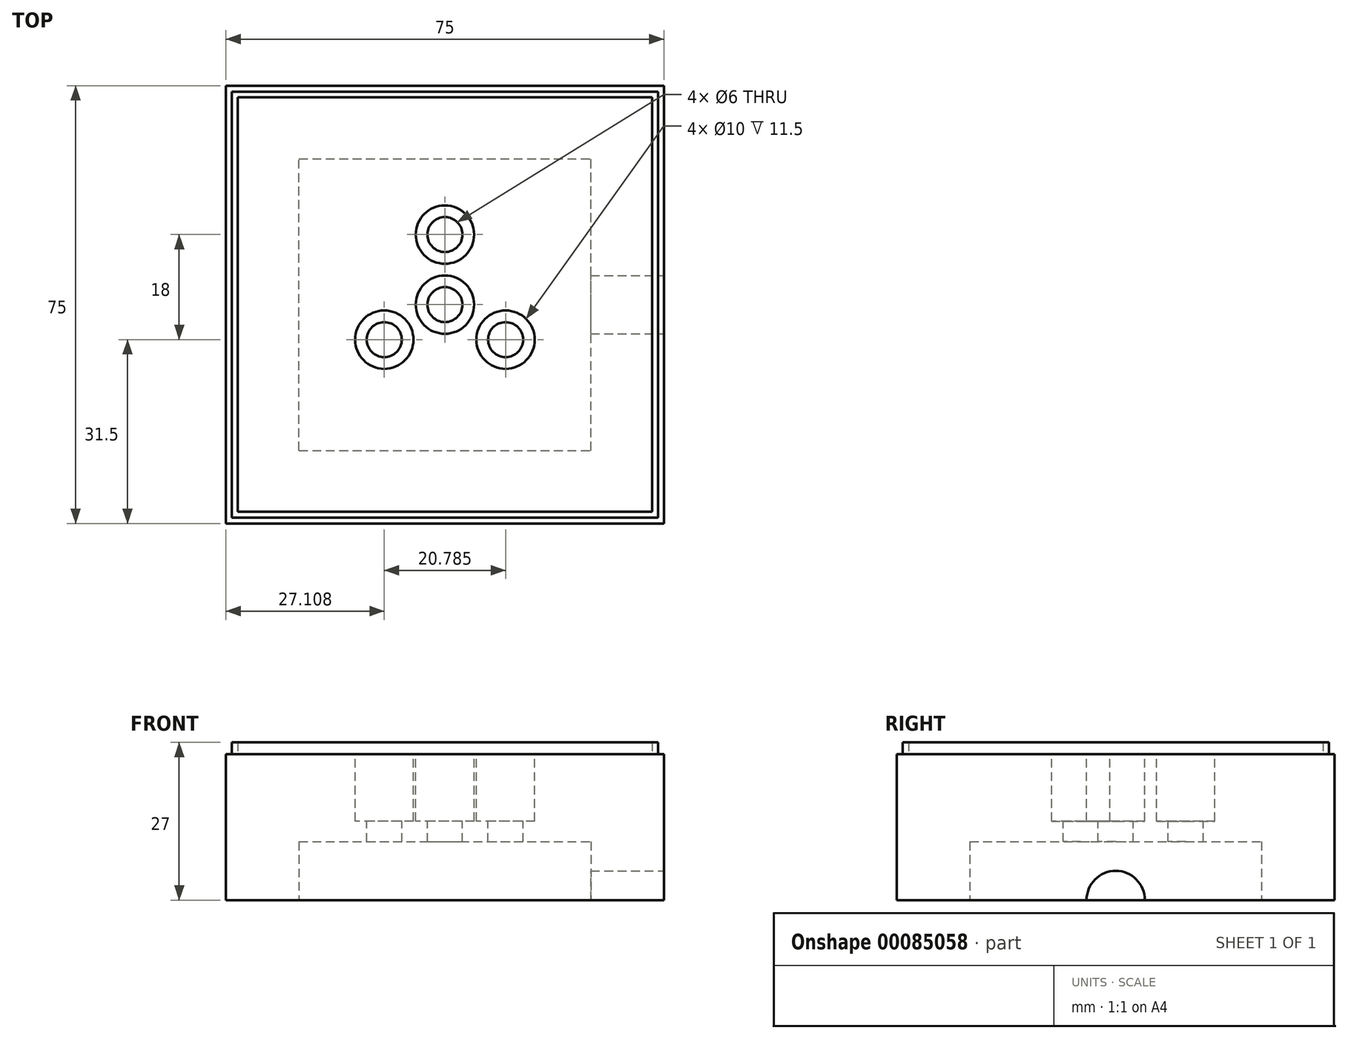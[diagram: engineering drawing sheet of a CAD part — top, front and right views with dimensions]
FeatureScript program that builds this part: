
annotation { "Feature Type Name" : "Feature", "Feature Type Description" : "" }
export const myFeature = defineFeature(function(context is Context, id is Id, definition is map)
    precondition{}
    {
        {
            var Q0;
            Q0=qCreatedBy(makeId("Top.planeOp"),FACE);
            var sketch = newSketch(context, id + "F0", { "sketchPlane" : qUnion([Q0])});
            skLineSegment(sketch, "E0.bottom", {"start": v(37.5, 37.5) * mm, "end": v(-37.5, 37.5) * mm});
            skLineSegment(sketch, "E0.top", {"start": v(37.5, -37.5) * mm, "end": v(-37.5, -37.5) * mm});
            skLineSegment(sketch, "E0.left", {"start": v(37.5, 37.5) * mm, "end": v(37.5, -37.5) * mm});
            skLineSegment(sketch, "E0.right", {"start": v(-37.5, 37.5) * mm, "end": v(-37.5, -37.5) * mm});
            skPoint(sketch, "E0.middle", {"position": v(0, 0) * mm});
            skSolve(sketch);
        }
        {
            var Q0;
            Q0 = qSketchRegion(id + "F0", true);
            extrude(context, id + "F1", {"entities" : qUnion([Q0]), "depth" : 25 * mm});
        }
        {
            var Q0;
            Q0=makeQuery(id+"F1.opExtrude","CAP_FACE",FACE,{"disambiguationData":[OSD([sQuery(id+"F0.wireOp",EDGE,"E0.bottom"),sQuery(id+"F0.wireOp",EDGE,"E0.top"),sQuery(id+"F0.wireOp",EDGE,"E0.left"),sQuery(id+"F0.wireOp",EDGE,"E0.right")])],"isStart":false});
            var sketch = newSketch(context, id + "F2", { "sketchPlane" : qUnion([Q0])});
            skLineSegment(sketch, "E1.bottom", {"start": v(35.5, 35.5) * mm, "end": v(-35.5, 35.5) * mm});
            skLineSegment(sketch, "E1.top", {"start": v(35.5, -35.5) * mm, "end": v(-35.5, -35.5) * mm});
            skLineSegment(sketch, "E1.left", {"start": v(35.5, 35.5) * mm, "end": v(35.5, -35.5) * mm});
            skLineSegment(sketch, "E1.right", {"start": v(-35.5, 35.5) * mm, "end": v(-35.5, -35.5) * mm});
            skPoint(sketch, "E1.middle", {"position": v(0, 0) * mm});
            skLineSegment(sketch, "E2.0", {"start": v(36.5, 36.5) * mm, "end": v(-36.5, 36.5) * mm});
            skLineSegment(sketch, "E2.1", {"start": v(36.5, 36.5) * mm, "end": v(36.5, -36.5) * mm});
            skLineSegment(sketch, "E2.2", {"start": v(36.5, -36.5) * mm, "end": v(-36.5, -36.5) * mm});
            skLineSegment(sketch, "E2.3", {"start": v(-36.5, 36.5) * mm, "end": v(-36.5, -36.5) * mm});
            skSolve(sketch);
        }
        {
            var Q0;
            Q0 = qSketchRegion(id + "F2", true);
            extrude(context, id + "F3", {"entities" : qUnion([Q0]), "operationType" : NewBodyOperationType.ADD, "depth" : 2 * mm});
        }
        {
            var Q0;
            Q0=makeQuery(id+"F3.boolean.opBoolean","SPLIT",FACE,{"disambiguationData":[TD([makeQuery(id+"F3.opExtrude","SWEPT_FACE",FACE,{"disambiguationData":[OSD([sQuery(id+"F2.wireOp",EDGE,"E1.bottom")])]})])],"derivedFrom":makeQuery(id+"F1.opExtrude","CAP_FACE",FACE,{"disambiguationData":[OSD([sQuery(id+"F0.wireOp",EDGE,"E0.bottom"),sQuery(id+"F0.wireOp",EDGE,"E0.top"),sQuery(id+"F0.wireOp",EDGE,"E0.left"),sQuery(id+"F0.wireOp",EDGE,"E0.right")])],"isStart":false})});
            var sketch = newSketch(context, id + "F4", { "sketchPlane" : qUnion([Q0])});
            skCircle(sketch, "E3", {"center": v(0, 0) * mm, "radius": 3 * mm});
            skLineSegment(sketch, "E4", {"start": v(0, 0) * mm, "end": v(0, 12) * mm});
            skCircle(sketch, "E5", {"center": v(0, 12) * mm, "radius": 3 * mm});
            skCircle(sketch, "E6.1.0", {"center": v(-10.4, -6) * mm, "radius": 3 * mm});
            skCircle(sketch, "E6.2.0", {"center": v(10.4, -6) * mm, "radius": 3 * mm});
            skSolve(sketch);
        }
        {
            var Q0;
            Q0 = qSketchRegion(id + "F4", true);
            extrude(context, id + "F5", {"entities" : qUnion([Q0]), "operationType" : NewBodyOperationType.REMOVE, "oppositeDirection" : true, "depth" : 20 * mm});
        }
        {
            var Q0;
            Q0=makeQuery(id+"F3.boolean.opBoolean","SPLIT",FACE,{"disambiguationData":[TD([makeQuery(id+"F3.opExtrude","SWEPT_FACE",FACE,{"disambiguationData":[OSD([sQuery(id+"F2.wireOp",EDGE,"E1.bottom")])]})])],"derivedFrom":makeQuery(id+"F1.opExtrude","CAP_FACE",FACE,{"disambiguationData":[OSD([sQuery(id+"F0.wireOp",EDGE,"E0.bottom"),sQuery(id+"F0.wireOp",EDGE,"E0.top"),sQuery(id+"F0.wireOp",EDGE,"E0.left"),sQuery(id+"F0.wireOp",EDGE,"E0.right")])],"isStart":false})});
            var sketch = newSketch(context, id + "F6", { "sketchPlane" : qUnion([Q0])});
            skCircle(sketch, "E7", {"center": v(0, 0) * mm, "radius": 5 * mm});
            skCircle(sketch, "E8", {"center": v(0, 12) * mm, "radius": 5 * mm});
            skCircle(sketch, "E9.1.0", {"center": v(-10.4, -6) * mm, "radius": 5 * mm});
            skCircle(sketch, "E9.2.0", {"center": v(10.4, -6) * mm, "radius": 5 * mm});
            skSolve(sketch);
        }
        {
            var Q0;
            Q0 = qSketchRegion(id + "F6", true);
            extrude(context, id + "F7", {"entities" : qUnion([Q0]), "operationType" : NewBodyOperationType.REMOVE, "oppositeDirection" : true, "depth" : 11.5 * mm});
        }
        {
            var Q0;
            Q0=makeQuery(id+"F1.opExtrude","CAP_FACE",FACE,{"disambiguationData":[OSD([sQuery(id+"F0.wireOp",EDGE,"E0.bottom"),sQuery(id+"F0.wireOp",EDGE,"E0.top"),sQuery(id+"F0.wireOp",EDGE,"E0.left"),sQuery(id+"F0.wireOp",EDGE,"E0.right")])],"isStart":true});
            var sketch = newSketch(context, id + "F8", { "sketchPlane" : qUnion([Q0])});
            skLineSegment(sketch, "E10.bottom", {"start": v(-25, 25) * mm, "end": v(25, 25) * mm});
            skLineSegment(sketch, "E10.top", {"start": v(-25, -25) * mm, "end": v(25, -25) * mm});
            skLineSegment(sketch, "E10.left", {"start": v(-25, 25) * mm, "end": v(-25, -25) * mm});
            skLineSegment(sketch, "E10.right", {"start": v(25, 25) * mm, "end": v(25, -25) * mm});
            skPoint(sketch, "E10.middle", {"position": v(0, 0) * mm});
            skSolve(sketch);
        }
        {
            var Q0;
            Q0 = qSketchRegion(id + "F8", true);
            extrude(context, id + "F9", {"entities" : qUnion([Q0]), "operationType" : NewBodyOperationType.REMOVE, "oppositeDirection" : true, "depth" : 10 * mm});
        }
        {
            var Q0;
            Q0=makeQuery(id+"F1.opExtrude","SWEPT_FACE",FACE,{"disambiguationData":[OSD([sQuery(id+"F0.wireOp",EDGE,"E0.left")])]});
            var sketch = newSketch(context, id + "F10", { "sketchPlane" : qUnion([Q0])});
            skCircle(sketch, "E11", {"center": v(0, 0) * mm, "radius": 5 * mm});
            skSolve(sketch);
        }
        {
            var Q0;
            Q0 = qSketchRegion(id + "F10", true);
            extrude(context, id + "F11", {"entities" : qUnion([Q0]), "operationType" : NewBodyOperationType.REMOVE, "oppositeDirection" : true, "depth" : 15 * mm});
        }
    });
